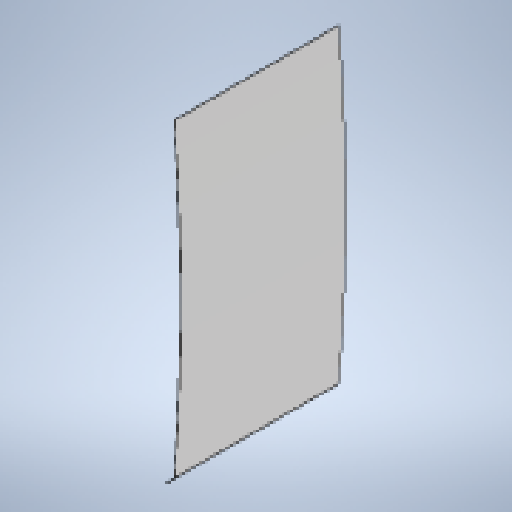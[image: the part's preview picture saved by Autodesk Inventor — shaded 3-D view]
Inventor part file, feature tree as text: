
AUTODESK INVENTOR PART (.ipt)
format: ipt  version: 2025 (Build 290162010, 162A)  size: 332,800 bytes
history: native  units: mm
features: other x4, sheet_metal_op x3, sketch x2
ambient origin geometry x8: Origin, YZ Plane, XZ Plane, XY Plane, X Axis, Y Axis, Z Axis, Center Point
bodies: Body1 (feature_tree)
feature tree (9):
  sheet_metal_op  "Contour Flange2"
  other  "Mark2"
  other  "A-Side Definition"
  sketch  "Sketch1"  dims[d36=3.0mm]
  other  "Plate2"
  sheet_metal_op  "Bend2"
  sheet_metal_op  "Corner2"
  sketch  "Sketch4"  dims[d37=3.0mm d38=1.5mm d39=6.0mm d40=5.0mm d41=980.0mm d42=5.0mm d43=3.0mm d44=12.0mm d45=3.0mm d46=5.0mm d65=8.0mm d78=3.0mm d80=3.0mm d121=5.0mm d122=63.0mm d123=11050.0mm d124=23.736478mm d125=1843.0mm d126=5.0mm d127=12.0mm d128=12.0mm d130=0.0mm]
  other  "Definition1"
